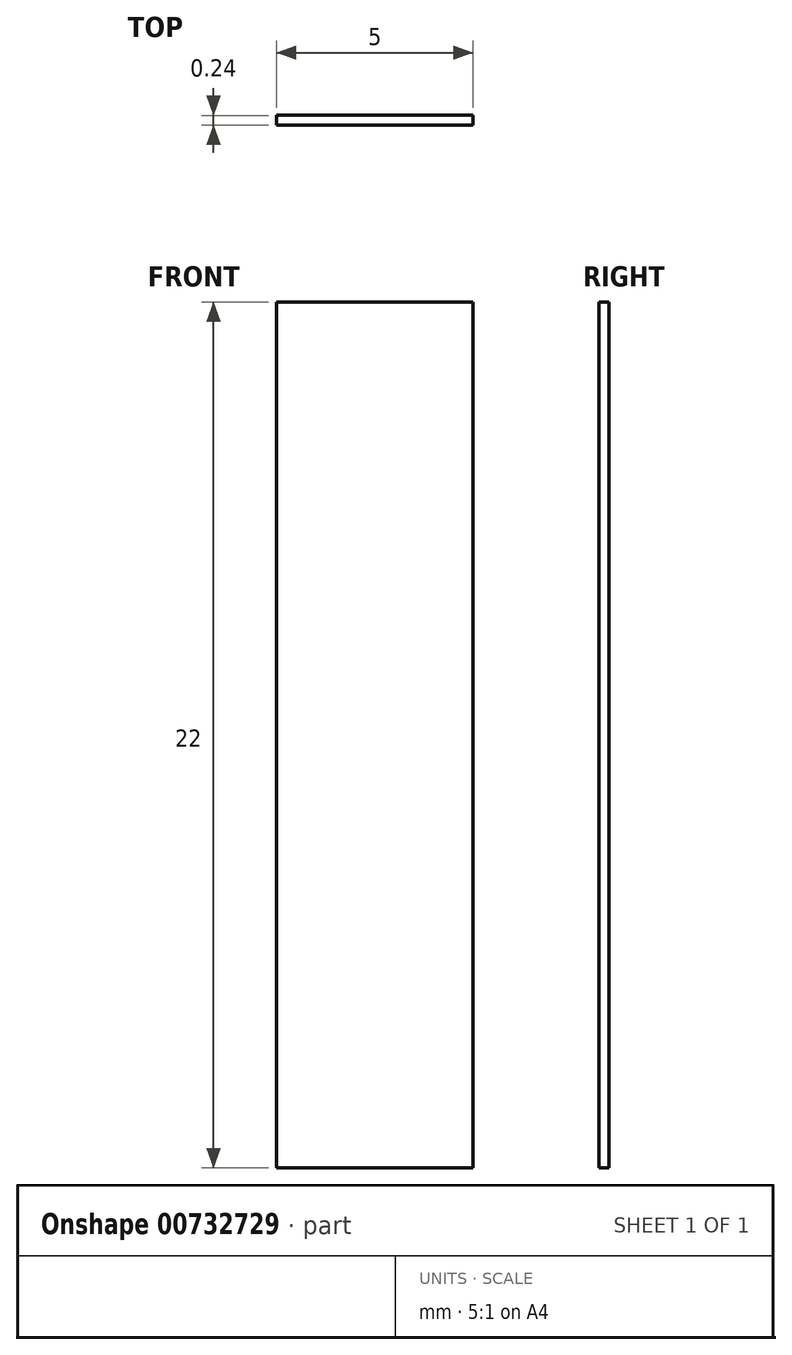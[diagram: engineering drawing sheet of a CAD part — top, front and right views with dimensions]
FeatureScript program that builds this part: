
annotation { "Feature Type Name" : "Feature", "Feature Type Description" : "" }
export const myFeature = defineFeature(function(context is Context, id is Id, definition is map)
    precondition{}
    {
        {
            var Q0;
            Q0=qCreatedBy(makeId("Top.planeOp"),FACE);
            var sketch = newSketch(context, id + "F0", { "sketchPlane" : qUnion([Q0])});
            skLineSegment(sketch, "E0.bottom", {"start": v(2.5, -0.12) * mm, "end": v(-2.5, -0.13) * mm});
            skLineSegment(sketch, "E0.top", {"start": v(2.5, 0.13) * mm, "end": v(-2.5, 0.12) * mm});
            skLineSegment(sketch, "E0.left", {"start": v(2.5, -0.12) * mm, "end": v(2.5, 0.13) * mm});
            skLineSegment(sketch, "E0.right", {"start": v(-2.5, -0.13) * mm, "end": v(-2.5, 0.12) * mm});
            skPoint(sketch, "E0.middle", {"position": v(0, 0) * mm});
            skSolve(sketch);
        }
        {
            var Q0;
            Q0=makeQuery(id+"F0.imprint","IMPRINT",FACE,{"disambiguationData":[TD([[makeQuery(id+"F0.imprint","IMPRINT",EDGE,{"derivedFrom":sQuery(id+"F0.wireOp",EDGE,"E0.bottom")}),-1.0]])]});
            extrude(context, id + "F1", {"entities" : qUnion([Q0]), "depth" : 22 * mm, "offsetDistance" : 25.4 * mm});
        }
    });
